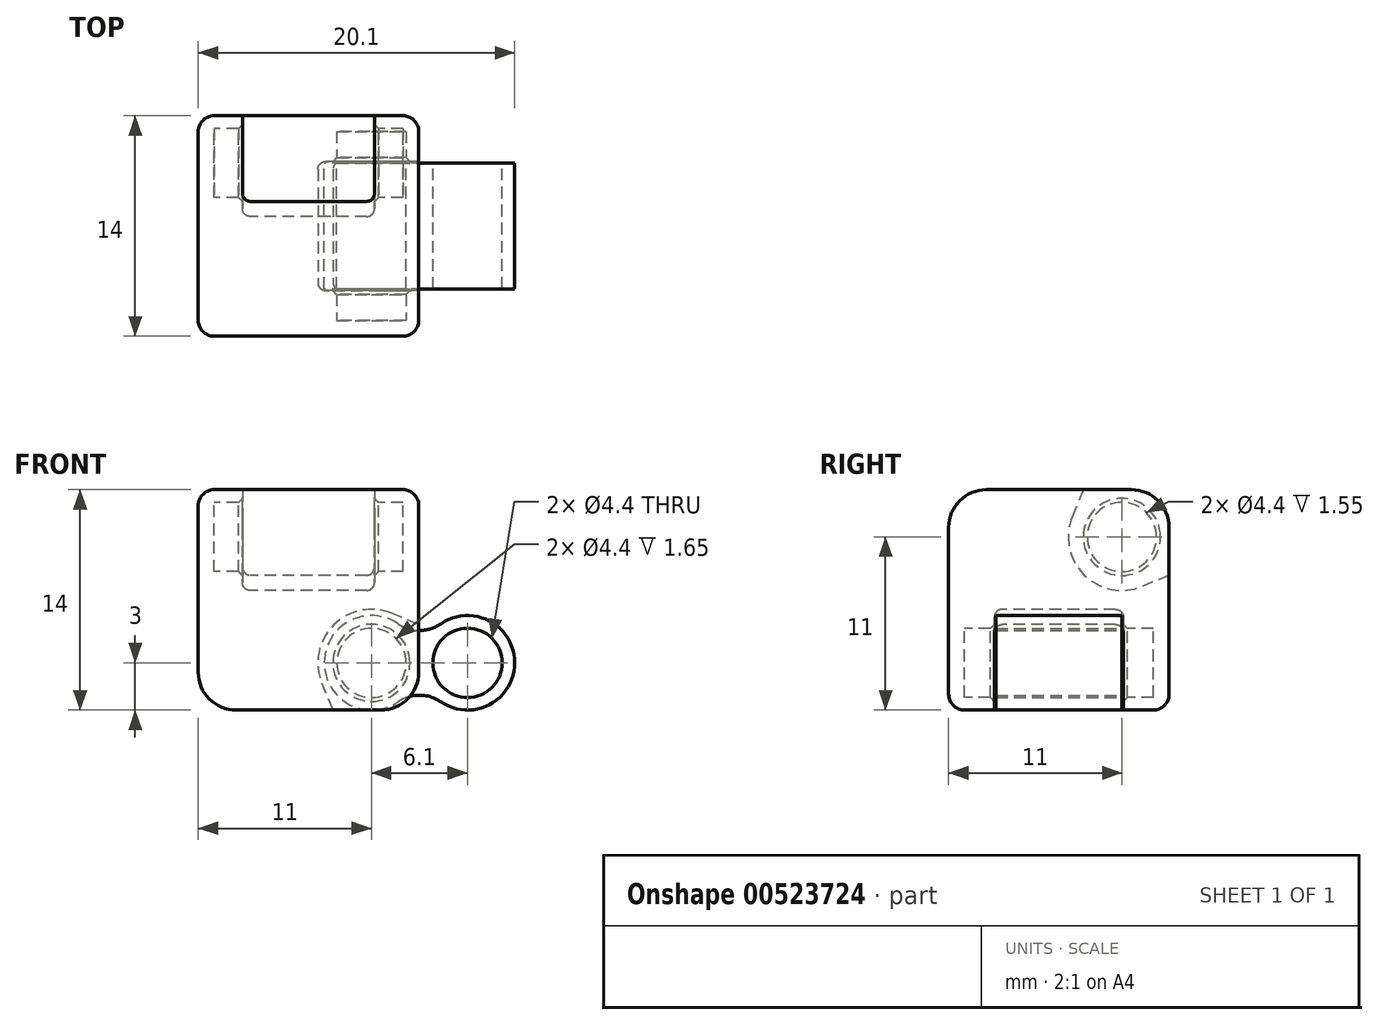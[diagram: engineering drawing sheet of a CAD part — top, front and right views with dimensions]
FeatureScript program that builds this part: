
annotation { "Feature Type Name" : "Feature", "Feature Type Description" : "" }
export const myFeature = defineFeature(function(context is Context, id is Id, definition is map)
    precondition{}
    {
        {
            assignVariable(context, id + "F0", {"name" : "magnetDiameter", "anyValue" : 4});
        }
        {
            assignVariable(context, id + "F1", {"name" : "magnetLength", "anyValue" : 4});
        }
        {
            assignVariable(context, id + "F2", {"name" : "extrusionWidth", "anyValue" : .4});
        }
        {
            assignVariable(context, id + "F3", {"name" : "cubeSize", "anyValue" : getVariable(context, 'magnetLength') * 3 + getVariable(context, 'extrusionWidth') * 5});
        }
        {
            var Q0;
            Q0=qCreatedBy(makeId("Top.planeOp"),FACE);
            var sketch = newSketch(context, id + "F4", { "sketchPlane" : qUnion([Q0])});
            skLineSegment(sketch, "E0.bottom", {"start": v(7, -7) * mm, "end": v(-7, -7) * mm});
            skLineSegment(sketch, "E0.top", {"start": v(7, 7) * mm, "end": v(-7, 7) * mm});
            skLineSegment(sketch, "E0.left", {"start": v(7, -7) * mm, "end": v(7, 7) * mm});
            skLineSegment(sketch, "E0.right", {"start": v(-7, -7) * mm, "end": v(-7, 7) * mm});
            skPoint(sketch, "E0.middle", {"position": v(0, 0) * mm});
            skSolve(sketch);
        }
        {
            var Q0;
            Q0=qSketchRegion(id+"F4",true);
            extrude(context, id + "F5", {"entities" : qUnion([Q0]), "depth" : (getVariable(context, 'cubeSize')) * mm, "offsetDistance" : 25 * mm});
        }
        {
            var Q0;
            Q0=qCreatedBy(makeId("Front.planeOp"),FACE);
            var sketch = newSketch(context, id + "F6", { "sketchPlane" : qUnion([Q0])});
            skCircle(sketch, "E1", {"center": v(4, 3) * mm, "radius": 2.2 * mm});
            skLineSegment(sketch, "E2", {"start": v(4, 3) * mm, "end": v(6.2, 3) * mm, "construction": true});
            skLineSegment(sketch, "E3", {"start": v(6.2, 3) * mm, "end": v(7, 3) * mm, "construction": true});
            skLineSegment(sketch, "E4", {"start": v(4, 0) * mm, "end": v(4, 0.8) * mm, "construction": true});
            skLineSegment(sketch, "E5", {"start": v(4, 0.8) * mm, "end": v(4, 3) * mm, "construction": true});
            skLineSegment(sketch, "E6", {"start": v(7, 0) * mm, "end": v(1.56, 0) * mm});
            skLineSegment(sketch, "E7", {"start": v(1.56, 0) * mm, "end": v(0.86, 1.7) * mm});
            skLineSegment(sketch, "E8", {"start": v(7, 0) * mm, "end": v(7, 5.44) * mm});
            skLineSegment(sketch, "E9", {"start": v(7, 5.44) * mm, "end": v(5.3, 6.14) * mm});
            skArc(sketch, "E10", {"start": v(5.3, 6.14) * mm, "mid": v(1.6, 5.4) * mm, "end": v(0.86, 1.7) * mm});
            skSolve(sketch);
        }
        {
            assignVariable(context, id + "F7", {"name" : "hingeSize", "anyValue" : getVariable(context, 'magnetLength') * 2});
        }
        {
            var Q0;
            Q0=makeQuery(id+"F6.imprint","IMPRINT",FACE,{"disambiguationData":[TD([[makeQuery(id+"F6.imprint","IMPRINT",EDGE,{"derivedFrom":sQuery(id+"F6.wireOp",EDGE,"E1")}),-1.0]])]});
            var Q1;
            Q1=makeQuery(id+"F6.imprint","IMPRINT",FACE,{"disambiguationData":[TD([[makeQuery(id+"F6.imprint","IMPRINT",EDGE,{"derivedFrom":sQuery(id+"F6.wireOp",EDGE,"E1")}),1.0]])]});
            extrude(context, id + "F8", {"entities" : qUnion([Q0, Q1]), "operationType" : NewBodyOperationType.REMOVE, "endBound" : BoundingType.SYMMETRIC, "oppositeDirection" : true, "depth" : (getVariable(context, 'hingeSize') + 0.2) * mm, "offsetDistance" : 25 * mm});
        }
        {
            var Q0;
            Q0=makeQuery(id+"F6.imprint","IMPRINT",FACE,{"disambiguationData":[TD([[makeQuery(id+"F6.imprint","IMPRINT",EDGE,{"derivedFrom":sQuery(id+"F6.wireOp",EDGE,"E1")}),1.0]])]});
            extrude(context, id + "F9", {"entities" : qUnion([Q0]), "operationType" : NewBodyOperationType.REMOVE, "endBound" : BoundingType.SYMMETRIC, "oppositeDirection" : true, "depth" : (getVariable(context, 'hingeSize') + getVariable(context, 'magnetLength')) * mm, "offsetDistance" : 25 * mm});
        }
        {
            var Q0;
            Q0=qCreatedBy(makeId("Right.planeOp"),FACE);
            var sketch = newSketch(context, id + "F10", { "sketchPlane" : qUnion([Q0])});
            skCircle(sketch, "E11", {"center": v(4, 11) * mm, "radius": 2.2 * mm});
            skLineSegment(sketch, "E12", {"start": v(1.56, 14) * mm, "end": v(7, 14) * mm});
            skLineSegment(sketch, "E13", {"start": v(7, 14) * mm, "end": v(7, 8.56) * mm});
            skLineSegment(sketch, "E14", {"start": v(7, 8.56) * mm, "end": v(5.3, 7.86) * mm});
            skLineSegment(sketch, "E15", {"start": v(1.56, 14) * mm, "end": v(0.86, 12.3) * mm});
            skLineSegment(sketch, "E16", {"start": v(4, 11) * mm, "end": v(6.2, 11) * mm, "construction": true});
            skLineSegment(sketch, "E17", {"start": v(6.2, 11) * mm, "end": v(7, 11) * mm, "construction": true});
            skLineSegment(sketch, "E18", {"start": v(4, 11) * mm, "end": v(4, 13.2) * mm, "construction": true});
            skLineSegment(sketch, "E19", {"start": v(4, 13.2) * mm, "end": v(4, 14) * mm, "construction": true});
            skArc(sketch, "E20", {"start": v(0.86, 12.3) * mm, "mid": v(1.6, 8.6) * mm, "end": v(5.3, 7.86) * mm});
            skSolve(sketch);
        }
        {
            var Q0;
            Q0=makeQuery(id+"F10.imprint","IMPRINT",FACE,{"disambiguationData":[TD([[makeQuery(id+"F10.imprint","IMPRINT",EDGE,{"derivedFrom":sQuery(id+"F10.wireOp",EDGE,"E11")}),1.0]])]});
            var Q1;
            Q1=makeQuery(id+"F10.imprint","IMPRINT",FACE,{"disambiguationData":[TD([[makeQuery(id+"F10.imprint","IMPRINT",EDGE,{"derivedFrom":sQuery(id+"F10.wireOp",EDGE,"E11")}),-1.0]])]});
            extrude(context, id + "F11", {"entities" : qUnion([Q0, Q1]), "operationType" : NewBodyOperationType.REMOVE, "endBound" : BoundingType.SYMMETRIC, "depth" : (getVariable(context, 'hingeSize') + 0.4) * mm, "offsetDistance" : 25 * mm});
        }
        {
            var Q0;
            Q0=makeQuery(id+"F10.imprint","IMPRINT",FACE,{"disambiguationData":[TD([[makeQuery(id+"F10.imprint","IMPRINT",EDGE,{"derivedFrom":sQuery(id+"F10.wireOp",EDGE,"E11")}),1.0]])]});
            extrude(context, id + "F12", {"entities" : qUnion([Q0]), "operationType" : NewBodyOperationType.REMOVE, "endBound" : BoundingType.SYMMETRIC, "depth" : (getVariable(context, 'hingeSize') + getVariable(context, 'magnetLength')) * mm, "offsetDistance" : 25 * mm});
        }
        {
            var Q0;
            {var subQ0=sQuery(id+"F4.wireOp",EDGE,"E0.bottom");var subQ1=sQuery(id+"F4.wireOp",EDGE,"E0.left");Q0=makeQuery(id+"F8.boolean.opBoolean","SPLIT",EDGE,{"disambiguationData":[TD([makeQuery(id+"F5.opExtrude","SWEPT_FACE",FACE,{"disambiguationData":[OSD([subQ0])]})])],"derivedFrom":makeQuery(id+"F5.opExtrude","CAP_EDGE",EDGE,{"disambiguationData":[OSD([subQ1])],"isStart":true})});}
            var Q1;
            {var subQ0=sQuery(id+"F4.wireOp",EDGE,"E0.left");var subQ1=sQuery(id+"F4.wireOp",EDGE,"E0.top");Q1=makeQuery(id+"F8.boolean.opBoolean","SPLIT",EDGE,{"disambiguationData":[TD([makeQuery(id+"F5.opExtrude","SWEPT_FACE",FACE,{"disambiguationData":[OSD([subQ1])]})])],"derivedFrom":makeQuery(id+"F5.opExtrude","CAP_EDGE",EDGE,{"disambiguationData":[OSD([subQ0])],"isStart":true})});}
            var Q2;
            {var subQ0=sQuery(id+"F4.wireOp",EDGE,"E0.right");var subQ1=sQuery(id+"F4.wireOp",EDGE,"E0.top");Q2=makeQuery(id+"F11.boolean.opBoolean","SPLIT",EDGE,{"disambiguationData":[TD([makeQuery(id+"F5.opExtrude","SWEPT_FACE",FACE,{"disambiguationData":[OSD([subQ0])]})])],"derivedFrom":makeQuery(id+"F5.opExtrude","CAP_EDGE",EDGE,{"disambiguationData":[OSD([subQ1])],"isStart":false})});}
            var Q3;
            {var subQ0=sQuery(id+"F4.wireOp",EDGE,"E0.left");var subQ1=sQuery(id+"F4.wireOp",EDGE,"E0.top");Q3=makeQuery(id+"F11.boolean.opBoolean","SPLIT",EDGE,{"disambiguationData":[TD([makeQuery(id+"F5.opExtrude","SWEPT_FACE",FACE,{"disambiguationData":[OSD([subQ0])]})])],"derivedFrom":makeQuery(id+"F5.opExtrude","CAP_EDGE",EDGE,{"disambiguationData":[OSD([subQ1])],"isStart":false})});}
            var Q4;
            Q4=makeQuery(id+"F5.opExtrude","CAP_EDGE",EDGE,{"disambiguationData":[OSD([sQuery(id+"F4.wireOp",EDGE,"E0.bottom")])],"isStart":false});
            var Q5;
            Q5=makeQuery(id+"F5.opExtrude","CAP_EDGE",EDGE,{"disambiguationData":[OSD([sQuery(id+"F4.wireOp",EDGE,"E0.right")])],"isStart":true});
            fillet(context, id + "F13", {"entities" : qUnion([Q0, Q1, Q2, Q3, Q4, Q5]), "radius" : (getVariable(context, 'magnetDiameter') / 2 + getVariable(context, 'extrusionWidth')) * mm, "tangentPropagation" : true, "allowEdgeOverflow" : false});
        }
        {
            var Q0;
            Q0=makeQuery(id+"F8.boolean.opBoolean","COPY",EDGE,{"derivedFrom":makeQuery(id+"F8.opExtrude","CAP_EDGE",EDGE,{"disambiguationData":[OSD([sQuery(id+"F6.wireOp",EDGE,"E7")])],"isStart":true})});
            var Q1;
            Q1=makeQuery(id+"F8.boolean.opBoolean","COPY",EDGE,{"derivedFrom":makeQuery(id+"F8.opExtrude","CAP_EDGE",EDGE,{"disambiguationData":[OSD([sQuery(id+"F6.wireOp",EDGE,"E7")])],"isStart":false})});
            var Q2;
            Q2=makeQuery(id+"F11.boolean.opBoolean","COPY",EDGE,{"derivedFrom":makeQuery(id+"F11.opExtrude","CAP_EDGE",EDGE,{"disambiguationData":[OSD([sQuery(id+"F10.wireOp",EDGE,"E14")])],"isStart":false})});
            var Q3;
            Q3=makeQuery(id+"F11.boolean.opBoolean","COPY",EDGE,{"derivedFrom":makeQuery(id+"F11.opExtrude","CAP_EDGE",EDGE,{"disambiguationData":[OSD([sQuery(id+"F10.wireOp",EDGE,"E14")])],"isStart":true})});
            fillet(context, id + "F14", {"entities" : qUnion([Q0, Q1, Q2, Q3]), "radius" : .5 * mm, "tangentPropagation" : true, "allowEdgeOverflow" : false});
        }
        {
            var Q0;
            Q0=qCreatedBy(makeId("Front.planeOp"),FACE);
            var sketch = newSketch(context, id + "F15", { "sketchPlane" : qUnion([Q0])});
            skCircle(sketch, "E21", {"center": v(4, 3) * mm, "radius": 2.2 * mm});
            skArc(sketch, "E22", {"start": v(5.7, 5.48) * mm, "mid": v(1, 3) * mm, "end": v(5.7, 0.52) * mm});
            skArc(sketch, "E23", {"start": v(8.4, 0.52) * mm, "mid": v(13.1, 3) * mm, "end": v(8.4, 5.48) * mm});
            skLineSegment(sketch, "E24", {"start": v(4, 3) * mm, "end": v(7, 3) * mm, "construction": true});
            skCircle(sketch, "E25", {"center": v(10.1, 3) * mm, "radius": 2.2 * mm});
            skLineSegment(sketch, "E26", {"start": v(7, 3) * mm, "end": v(7.1, 3) * mm, "construction": true});
            skLineSegment(sketch, "E27", {"start": v(7.1, 3) * mm, "end": v(10.1, 3) * mm, "construction": true});
            skArc(sketch, "E28", {"start": v(5.7, 5.48) * mm, "mid": v(7.05, 5.06) * mm, "end": v(8.4, 5.48) * mm});
            skArc(sketch, "E29", {"start": v(8.4, 0.52) * mm, "mid": v(7.05, 0.94) * mm, "end": v(5.7, 0.52) * mm});
            skLineSegment(sketch, "E30", {"start": v(7.05, -1.46) * mm, "end": v(7.05, 3) * mm, "construction": true});
            skLineSegment(sketch, "E31", {"start": v(7.05, 3) * mm, "end": v(7.05, 7.46) * mm, "construction": true});
            skSolve(sketch);
        }
        {
            var Q0;
            Q0=makeQuery(id+"F15.imprint","IMPRINT",FACE,{"disambiguationData":[TD([[makeQuery(id+"F15.imprint","IMPRINT",EDGE,{"derivedFrom":sQuery(id+"F15.wireOp",EDGE,"E21")}),-1.0]])]});
            extrude(context, id + "F16", {"entities" : qUnion([Q0]), "endBound" : BoundingType.SYMMETRIC, "depth" : (getVariable(context, 'hingeSize')) * mm, "offsetDistance" : 25 * mm});
        }
        {
            var Q0;
            Q0=makeQuery(id+"F9.boolean.opBoolean","INTERSECT",EDGE,{"derivedFrom":[makeQuery(id+"F8.boolean.opBoolean","COPY",FACE,{"derivedFrom":makeQuery(id+"F8.opExtrude","CAP_FACE",FACE,{"disambiguationData":[OSD([sQuery(id+"F6.wireOp",EDGE,"E6"),sQuery(id+"F6.wireOp",EDGE,"E7"),sQuery(id+"F6.wireOp",EDGE,"E8"),sQuery(id+"F6.wireOp",EDGE,"E9"),sQuery(id+"F6.wireOp",EDGE,"E10")])],"isStart":false})}),makeQuery(id+"F9.opExtrude","SWEPT_FACE",FACE,{"disambiguationData":[OSD([sQuery(id+"F6.wireOp",EDGE,"E1")])]})]});
            var Q1;
            Q1=makeQuery(id+"F9.boolean.opBoolean","INTERSECT",EDGE,{"derivedFrom":[makeQuery(id+"F8.boolean.opBoolean","COPY",FACE,{"derivedFrom":makeQuery(id+"F8.opExtrude","CAP_FACE",FACE,{"disambiguationData":[OSD([sQuery(id+"F6.wireOp",EDGE,"E6"),sQuery(id+"F6.wireOp",EDGE,"E7"),sQuery(id+"F6.wireOp",EDGE,"E8"),sQuery(id+"F6.wireOp",EDGE,"E9"),sQuery(id+"F6.wireOp",EDGE,"E10")])],"isStart":true})}),makeQuery(id+"F9.opExtrude","SWEPT_FACE",FACE,{"disambiguationData":[OSD([sQuery(id+"F6.wireOp",EDGE,"E1")])]})]});
            var Q2;
            Q2=makeQuery(id+"F12.boolean.opBoolean","INTERSECT",EDGE,{"derivedFrom":[makeQuery(id+"F11.boolean.opBoolean","COPY",FACE,{"derivedFrom":makeQuery(id+"F11.opExtrude","CAP_FACE",FACE,{"disambiguationData":[OSD([sQuery(id+"F10.wireOp",EDGE,"E12"),sQuery(id+"F10.wireOp",EDGE,"E13"),sQuery(id+"F10.wireOp",EDGE,"E14"),sQuery(id+"F10.wireOp",EDGE,"E15"),sQuery(id+"F10.wireOp",EDGE,"E20")])],"isStart":true})}),makeQuery(id+"F12.opExtrude","SWEPT_FACE",FACE,{"disambiguationData":[OSD([sQuery(id+"F10.wireOp",EDGE,"E11")])]})]});
            var Q3;
            Q3=makeQuery(id+"F12.boolean.opBoolean","INTERSECT",EDGE,{"derivedFrom":[makeQuery(id+"F11.boolean.opBoolean","COPY",FACE,{"derivedFrom":makeQuery(id+"F11.opExtrude","CAP_FACE",FACE,{"disambiguationData":[OSD([sQuery(id+"F10.wireOp",EDGE,"E12"),sQuery(id+"F10.wireOp",EDGE,"E13"),sQuery(id+"F10.wireOp",EDGE,"E14"),sQuery(id+"F10.wireOp",EDGE,"E15"),sQuery(id+"F10.wireOp",EDGE,"E20")])],"isStart":false})}),makeQuery(id+"F12.opExtrude","SWEPT_FACE",FACE,{"disambiguationData":[OSD([sQuery(id+"F10.wireOp",EDGE,"E11")])]})]});
            chamfer(context, id + "F17", {"entities" : qUnion([Q0, Q1, Q2, Q3]), "width" : .25 * mm, "tangentPropagation" : true});
        }
        {
            var Q0;
            Q0=makeQuery(id+"F5.opExtrude","CAP_EDGE",EDGE,{"disambiguationData":[OSD([sQuery(id+"F4.wireOp",EDGE,"E0.right")])],"isStart":false});
            fillet(context, id + "F18", {"entities" : qUnion([Q0]), "radius" : 1 * mm, "tangentPropagation" : true, "allowEdgeOverflow" : false});
        }
    });
